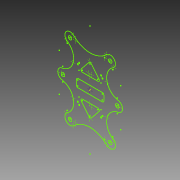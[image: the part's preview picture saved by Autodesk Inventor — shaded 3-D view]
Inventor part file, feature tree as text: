
AUTODESK INVENTOR PART (.ipt)
format: ipt  version: 2015 (Build 190159000, 159)  size: 94,208 bytes
history: native  units: mm
features: sketch x1
ambient origin geometry x8: Origin, YZ Plane, XZ Plane, XY Plane, X Axis, Y Axis, Z Axis, Center Point
feature tree (1):
  sketch  "Sketch1"  dims[d19=46.65mm]
